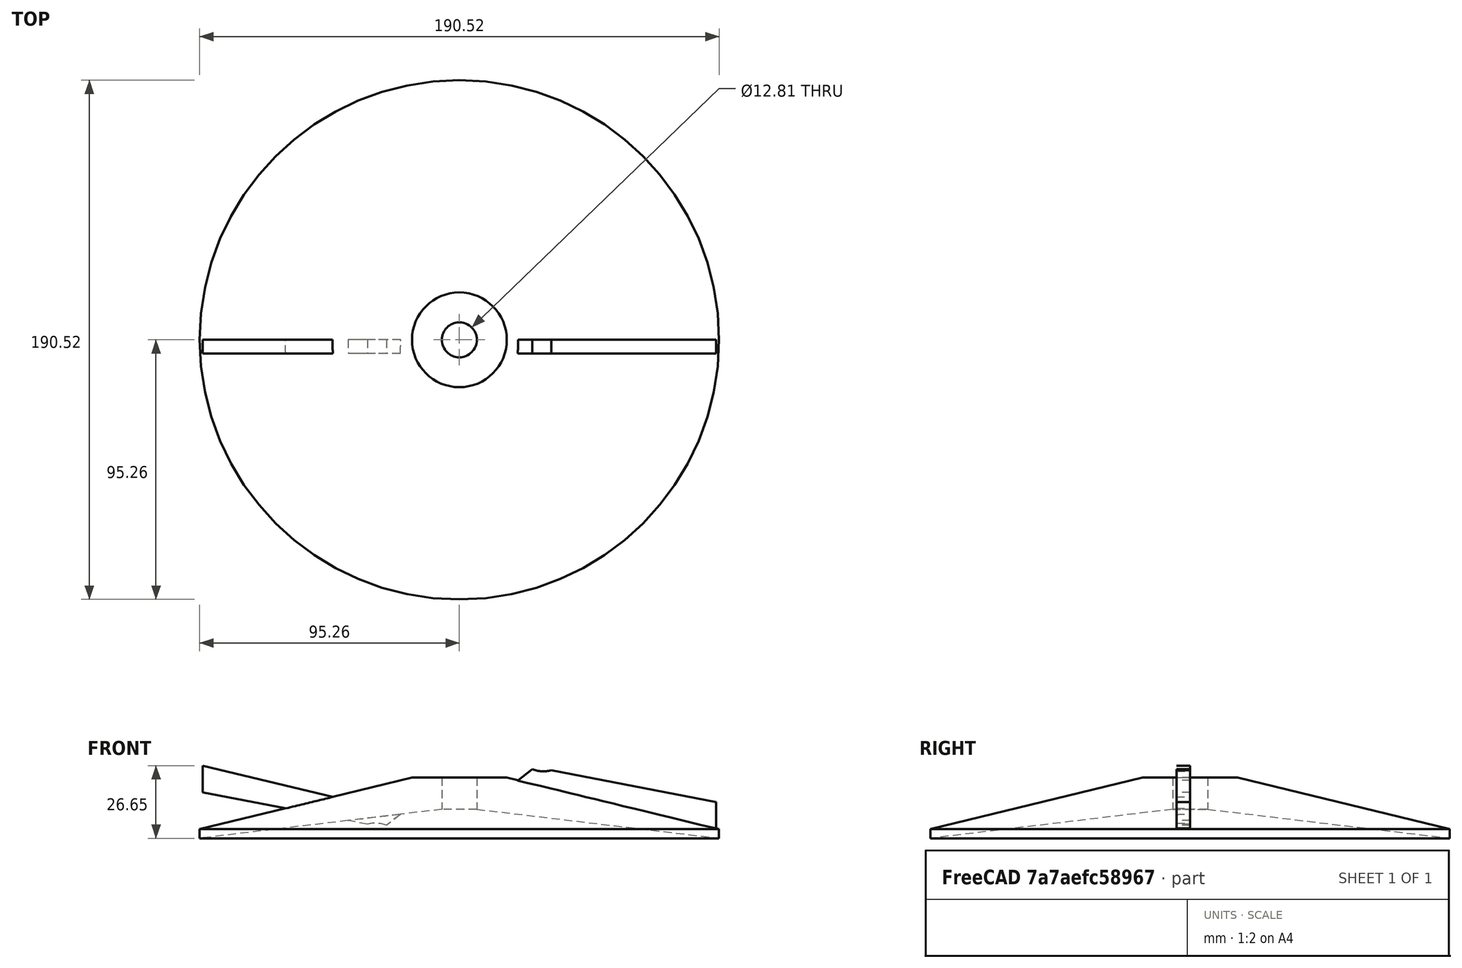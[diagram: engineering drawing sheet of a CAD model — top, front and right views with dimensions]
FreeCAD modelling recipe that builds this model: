
FCSTD DOCUMENT  (FreeCAD 0.21R33771 (Git))
Label: krilchatka1
License: All rights reserved
LicenseURL: http://en.wikipedia.org/wiki/All_rights_reserved
objects: Sketcher::SketchObject×2, PartDesign::Revolution×1, PartDesign::Pad×1, PartDesign::PolarPattern×1, PartDesign::Body×1
note: 8 computed .brp shape members not serialized (recipe doc carries the construction recipe); baked Part::Feature solids carry a one-line shape summary decoded from their .brp

FEATURE [Sketcher::SketchObject] Sketch
  FullyConstrained = false
  MapMode = 5
  Placement = pos=(0,0,0) rot=(1,0,0;1.5708rad)
  Support = -> [XZ_Plane]
  sketch-geometry (5):
    g0: LineSegment StartX=6.40599 StartY=7.23794 StartZ=0 EndX=6.40599 EndY=-4.40931 EndZ=0
    g1: LineSegment StartX=6.40599 StartY=-4.40931 StartZ=0 EndX=95.2579 EndY=-15.0582 EndZ=0
    g2: LineSegment StartX=6.40599 StartY=7.23794 StartZ=0 EndX=17.3877 EndY=7.23794 EndZ=0
    g3: LineSegment StartX=17.3877 StartY=7.23794 StartZ=0 EndX=95.2579 EndY=-11.7304 EndZ=0
    g4: LineSegment StartX=95.2579 StartY=-11.7304 StartZ=0 EndX=95.2579 EndY=-15.0582 EndZ=0
  constraints (8):
    c: Vertical(g0)
    c: Coincident(g2,g0)
    c: Horizontal(g2)
    c: Coincident(g4,g3)
    c: Coincident(g4,g1)
    c: Vertical(g4)
    c: Coincident(g0,g1)
    c: Coincident(g3,g2)
FEATURE [PartDesign::Revolution] Revolution
  Angle = 360
  Axis = (0,2e-16,1)
  Base = (0,0,0)
  Placement = pos=(0,0,0) rot=(1,0,0;1.5708rad)
  Profile = -> Sketch
  ReferenceAxis = -> Sketch [V_Axis]
  Refine = true
  Reversed = true
FEATURE [Sketcher::SketchObject] Sketch001
  FullyConstrained = false
  MapMode = 5
  Placement = pos=(0,0,0) rot=(1,0,0;1.5708rad)
  Support = -> [XZ_Plane]
  sketch-geometry (5):
    g0: LineSegment StartX=21.2205 StartY=5.96109 StartZ=0 EndX=26.6972 EndY=10.3385 EndZ=0
    g1: ArcOfCircle CenterX=30.801 CenterY=20.2099 CenterZ=0 NormalX=0 NormalY=0 NormalZ=1 AngleXU=0 Radius=10.6905 StartAngle=4.3184 EndAngle=4.98624
    g2: LineSegment StartX=33.6921 StartY=9.91776 StartZ=0 EndX=94.1177 EndY=-1.79532 EndZ=0
    g3: LineSegment StartX=94.1177 StartY=-1.79532 StartZ=0 EndX=94.1177 EndY=-11.5907 EndZ=0
    g4: LineSegment StartX=21.2205 StartY=5.96109 StartZ=0 EndX=94.1177 EndY=-11.5907 EndZ=0
  constraints (6):
    c: Coincident(g3,g2)
    c: Vertical(g3)
    c: Coincident(g4,g0)
    c: Coincident(g4,g3)
    c: Coincident(g1,g2)
    c: Coincident(g1,g0)
FEATURE [PartDesign::Pad] Pad
  BaseFeature = -> Revolution
  Direction = (0,-1,2e-16)
  Length = 5
  Length2 = 10
  Placement = pos=(0,0,0) rot=(1,0,0;1.5708rad)
  Profile = -> Sketch001
  ReferenceAxis = -> Sketch001 [N_Axis]
  Refine = true
  Type = 0
FEATURE [PartDesign::PolarPattern] PolarPattern
  Angle = 360
  Axis = -> Z_Axis
  BaseFeature = -> Pad
  Occurrences = 12
  Originals = -> [Pad]
  Placement = pos=(0,0,0) rot=(1,0,0;1.5708rad)
  Refine = true
FEATURE [PartDesign::Body] Body
  Group = -> [Sketch,Revolution,Sketch001,Pad,PolarPattern]
  Origin = -> Origin
  Tip = -> PolarPattern
